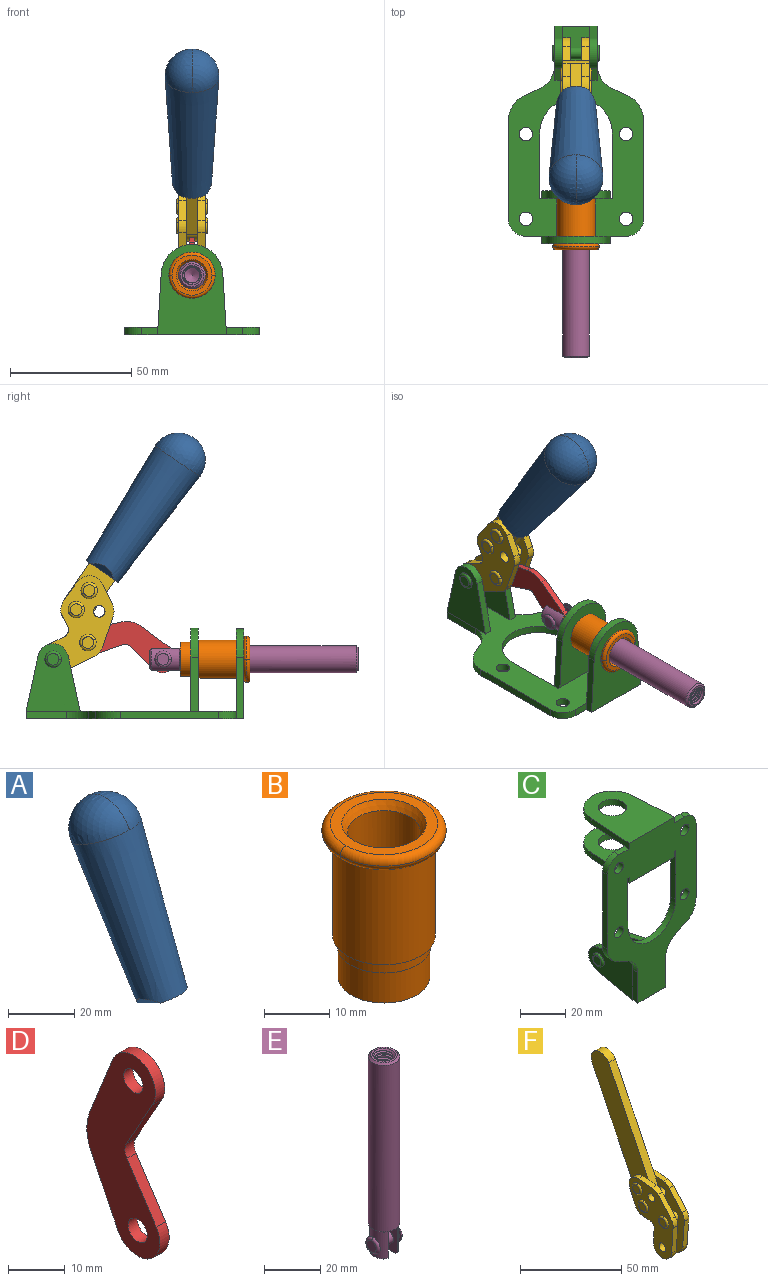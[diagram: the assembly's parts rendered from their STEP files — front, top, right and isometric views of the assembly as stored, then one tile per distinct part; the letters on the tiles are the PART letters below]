
ASSEMBLY  parts=6 mates=6
PART A: 11 faces, bbox 22.3x42.6x64.5 mm
  f0: sphere r=11.13mm, area 411.4mm2, adj f1,f8
  f1: cone r=11.11mm half-angle=3.3deg, axis (0,0.44,0.9), area 3251.8mm2, adj f0,f7,f8,f9,f10
  f2: cylinder r=6.16mm len=11.7mm, axis (1,0,0), area 89.5mm2, adj f3,f4,f5,f6
  f3: plane 60.23x36.75mm, normal (-1,0,0), area 763.6mm2, adj f2,f4,f6,f10
  f4: plane 51.37x25.05mm, normal (0,0.9,-0.44), area 264.2mm2, adj f2,f3,f5,f10
  f5: plane 60.23x36.75mm, normal (1,0,0), area 763.6mm2, adj f2,f4,f6,f10
  f6: plane 51.37x25.05mm, normal (0,-0.9,0.44), area 264.2mm2, adj f2,f3,f5,f10
  f7: plane 9.95x5.95mm, normal (0.71,-0.31,-0.64), area 25.8mm2, adj f1,f10
  f8: sphere r=11.13mm, area 411.4mm2, adj f0,f1
  f9: plane 9.95x5.95mm, normal (-0.71,-0.31,-0.64), area 25.8mm2, adj f1,f10
  f10: plane 14.27x11.38mm, normal (0,-0.44,-0.9), area 106.7mm2, adj f1,f3,f4,f5,f6,f7,f9
PART B: 15 faces, bbox 20.6x20.6x28.7 mm
  f0: torus R=8.26mm, axis (0,0,1), area 56.8mm2, adj f1,f10,f12
  f1: torus R=8.26mm, axis (0,0,1), area 56.8mm2, adj f0,f6,f13
  f2: cylinder r=5.59mm len=25.91mm, axis (0,0,1), area 909.6mm2, adj f3,f4
  f3: cone r=6.86mm half-angle=45deg, axis (0,0,-1), area 70.2mm2, adj f2,f14
  f4: cone r=6.47mm half-angle=30deg, axis (0,0,1), area 66.7mm2, adj f2,f13
  f5: cylinder r=7.04mm len=14.07mm, axis (0,0,1), area 252.6mm2, adj f11,f14
  f6: torus R=8.26mm, axis (0,0,1), area 56.8mm2, adj f1,f12,f13
  f7: cylinder r=7.16mm len=14.33mm, axis (0,0,1), area 91.5mm2, adj f9,f11
  f8: cylinder r=7.86mm len=18.42mm, axis (0,0,1), area 909.6mm2, adj f9,f10
  f9: plane 15.72x15.72mm, normal (0,0,-1), area 33mm2, adj f7,f8
  f10: plane 16.51x16.51mm, normal (0,0,-1), area 19.9mm2, adj f0,f8,f12
  f11: plane 14.33x14.33mm, normal (0,0,-1), area 5.7mm2, adj f5,f7
  f12: torus R=8.26mm, axis (0,0,1), area 56.8mm2, adj f0,f6,f10
  f13: plane 16.51x16.51mm, normal (0,0,1), area 82.7mm2, adj f1,f4,f6
  f14: plane 14.07x14.07mm, normal (0,0,-1), area 7.8mm2, adj f3,f5
PART C: 55 faces, bbox 55.7x37.4x89.8 mm
  f0: torus R=2.41mm, axis (-1,0,0), area 15mm2, adj f11,f15,f25
  f1: torus R=2.41mm, axis (-1,0,0), area 15mm2, adj f10,f12,f22
  f2: cylinder r=2.78mm len=5.56mm, axis (0,-1,0), area 54.2mm2, adj f30,f54
  f3: cylinder r=14.99mm len=29.97mm, axis (0,-1,0), area 145.9mm2, adj f30,f49,f53,f54
  f4: cylinder r=2.78mm len=5.56mm, axis (0,-1,0), area 54.2mm2, adj f30,f54
  f5: cylinder r=2.78mm len=5.56mm, axis (0,-1,0), area 54.2mm2, adj f30,f54
  f6: cylinder r=2.78mm len=5.56mm, axis (0,-1,0), area 54.2mm2, adj f30,f54
  f7: cylinder r=6.35mm len=12.7mm, axis (0,0,1), area 123.6mm2, adj f27,f51
  f8: cylinder r=6.35mm len=12.7mm, axis (0,0,-1), area 124.7mm2, adj f21,f35
  f9: cylinder r=2.41mm len=11.18mm, axis (-1,0,0), area 169.4mm2, adj f16,f19
  f10: plane 4.83x4.83mm, normal (1,0,0), area 18.3mm2, adj f1,f12
  f11: plane 4.83x4.83mm, normal (-1,0,0), area 18.3mm2, adj f0,f15
  f12: torus R=2.41mm, axis (-1,0,0), area 15mm2, adj f1,f10,f22
  f13: cylinder r=6.35mm len=12.41mm, axis (1,0,0), area 53.4mm2, adj f18,f19,f22,f23
  f14: cylinder r=6.35mm len=12.41mm, axis (-1,0,0), area 53.4mm2, adj f16,f17,f24,f25
  f15: torus R=2.41mm, axis (-1,0,0), area 15mm2, adj f0,f11,f25
  f16: plane 27.86x22.35mm, normal (1,0,0), area 425.4mm2, adj f9,f14,f17,f24,f30
  f17: plane 22.86x4.97mm, normal (0,0.21,0.98), area 72.5mm2, adj f14,f16,f25,f30
  f18: plane 22.86x4.97mm, normal (0,0.21,0.98), area 72.5mm2, adj f13,f19,f22,f30
  f19: plane 27.86x22.35mm, normal (-1,0,0), area 425.4mm2, adj f9,f13,f18,f23,f30
  f20: cylinder r=12.7mm len=25.35mm, axis (0,0,-1), area 119.8mm2, adj f21,f34,f35,f36
  f21: plane 34.21x28.07mm, normal (0,0,-1), area 702.4mm2, adj f8,f20,f30,f34,f36
  f22: plane 27.96x22.45mm, normal (1,0,0), area 407.2mm2, adj f1,f12,f13,f18,f23,f30,f42,f43
  f23: plane 22.86x4.97mm, normal (0,0.21,-0.98), area 72.5mm2, adj f13,f19,f22,f44
  f24: plane 22.86x4.97mm, normal (0,0.21,-0.98), area 72.5mm2, adj f14,f16,f25,f44
  f25: plane 27.86x22.35mm, normal (-1,0,0), area 407.1mm2, adj f0,f14,f15,f17,f24,f30,f45,f46
  f26: plane 3.1x0.95mm, normal (0,0,-1), area 2.7mm2, adj f30,f49,f50,f54
  f27: plane 34.21x28.07mm, normal (0,0,1), area 702.4mm2, adj f7,f28,f30,f50,f52
  f28: cylinder r=12.7mm len=25.35mm, axis (0,0,1), area 118.8mm2, adj f27,f50,f51,f52
  f29: plane 3.1x0.95mm, normal (0,0,-1), area 2.7mm2, adj f30,f52,f53,f54
  f30: plane 86.54x55.63mm, normal (0,1,0), area 2362.9mm2, adj f2,f3,f4,f5,f6,f16,f17,f18
  f31: plane 40.56x3.1mm, normal (-1,0,0), area 125.7mm2, adj f30,f32,f48,f54
  f32: cylinder r=7.11mm len=7.11mm, axis (0,-1,0), area 34.6mm2, adj f30,f31,f33,f54
  f33: plane 6.67x3.1mm, normal (0,0,1), area 20.4mm2, adj f30,f32,f34,f54
  f34: plane 25.39x3.13mm, normal (-1,0.06,0), area 79.5mm2, adj f20,f21,f33,f35,f54
  f35: plane 37.31x28.45mm, normal (0,0,1), area 789.9mm2, adj f8,f20,f34,f36,f54
  f36: plane 25.39x3.13mm, normal (1,0.06,0), area 79.5mm2, adj f20,f21,f35,f37,f54
  f37: plane 6.67x3.1mm, normal (0,0,1), area 20.4mm2, adj f30,f36,f38,f54
  f38: cylinder r=7.11mm len=7.11mm, axis (0,-1,0), area 34.6mm2, adj f30,f37,f39,f54
  f39: plane 40.56x3.1mm, normal (1,0,0), area 125.7mm2, adj f30,f38,f40,f54
  f40: cylinder r=11.18mm len=10.16mm, axis (0,-1,0), area 39.5mm2, adj f30,f39,f41,f54
  f41: plane 6.09x3.1mm, normal (0.42,0,-0.91), area 20.8mm2, adj f30,f40,f42,f54
  f42: cylinder r=11.18mm len=9.41mm, axis (0,-1,0), area 37.2mm2, adj f22,f30,f41,f43,f54
  f43: plane 16.5x3.1mm, normal (1,0,0), area 51.1mm2, adj f22,f42,f44,f54
  f44: plane 17.37x3.1mm, normal (0,0,-1), area 53.8mm2, adj f23,f24,f30,f43,f45,f54
  f45: plane 16.5x3.1mm, normal (-1,0,0), area 51.1mm2, adj f25,f44,f46,f54
  f46: cylinder r=11.18mm len=9.41mm, axis (0,-1,0), area 37.2mm2, adj f25,f30,f45,f47,f54
  f47: plane 6.09x3.1mm, normal (-0.42,0,-0.91), area 20.8mm2, adj f30,f46,f48,f54
  f48: cylinder r=11.18mm len=10.16mm, axis (0,-1,0), area 39.5mm2, adj f30,f31,f47,f54
  f49: plane 26.54x3.1mm, normal (-1,0,0), area 82.3mm2, adj f3,f26,f30,f54
  f50: plane 25.39x3.1mm, normal (1,0.06,0), area 78.8mm2, adj f26,f27,f28,f51,f54
  f51: plane 37.31x28.45mm, normal (0,0,-1), area 789.9mm2, adj f7,f28,f50,f52,f54
  f52: plane 25.39x3.1mm, normal (-1,0.06,0), area 78.8mm2, adj f27,f28,f29,f51,f54
  f53: plane 26.54x3.1mm, normal (1,0,0), area 82.3mm2, adj f3,f29,f30,f54
  f54: plane 89.66x55.63mm, normal (0,-1,0), area 2678.5mm2, adj f2,f3,f4,f5,f6,f26,f29,f31
PART D: 12 faces, bbox 2.3x18.2x42.8 mm
  f0: cylinder r=2.4mm len=4.8mm, axis (1,0,0), area 34.9mm2, adj f4,f11
  f1: cylinder r=10.41mm len=8.47mm, axis (1,0,0), area 20.2mm2, adj f4,f9,f10,f11
  f2: cylinder r=3.05mm len=3.16mm, axis (1,0,0), area 7.7mm2, adj f4,f6,f7,f11
  f3: cylinder r=2.4mm len=4.8mm, axis (1,0,0), area 34.9mm2, adj f4,f11
  f4: plane 42.81x18.23mm, normal (-1,0,0), area 414.1mm2, adj f0,f1,f2,f3,f5,f6,f7,f8
  f5: cylinder r=5.54mm len=10.67mm, axis (1,0,0), area 41.8mm2, adj f4,f6,f10,f11
  f6: plane 11.66x6.53mm, normal (0,-0.87,-0.49), area 30.9mm2, adj f2,f4,f5,f11
  f7: plane 11.17x7.33mm, normal (0,-0.84,0.55), area 30.9mm2, adj f2,f4,f8,f11
  f8: cylinder r=5.54mm len=10.51mm, axis (1,0,0), area 41.8mm2, adj f4,f7,f9,f11
  f9: plane 13.67x6.67mm, normal (0,0.9,-0.44), area 35.1mm2, adj f1,f4,f8,f11
  f10: plane 14.1x5.7mm, normal (0,0.93,0.37), area 35.1mm2, adj f1,f4,f5,f11
  f11: plane 42.81x18.23mm, normal (1,0,0), area 414.1mm2, adj f0,f1,f2,f3,f5,f6,f7,f8
PART E: 48 faces, bbox 12.6x11.1x86.1 mm
  f0: torus R=2.41mm, axis (-1,0,0), area 15mm2, adj f30,f32,f34
  f1: torus R=2.41mm, axis (-1,0,0), area 15mm2, adj f29,f31,f33
  f2: cylinder r=5.54mm len=72.39mm, axis (0,0,1), area 2518.5mm2, adj f3,f4,f42,f43
  f3: cone r=5.54mm half-angle=45deg, axis (0,0,1), area 7.6mm2, adj f2,f5,f41
  f4: cone r=5.54mm half-angle=45deg, axis (0,0,-1), area 34.9mm2, adj f2,f39
  f5: cylinder r=5.08mm len=11.48mm, axis (0,0,1), area 108.3mm2, adj f3,f7,f8,f41
  f6: cylinder r=2.41mm len=4.83mm, axis (-1,0,0), area 71.2mm2, adj f40,f41
  f7: cylinder r=2.41mm len=4.83mm, axis (-1,0,0), area 7.6mm2, adj f5,f34
  f8: cone r=5.08mm half-angle=45deg, axis (0,0,1), area 10.6mm2, adj f5,f37,f41
  f9: cone r=3.98mm half-angle=45deg, axis (0,0,1), area 17.6mm2, adj f27,f39,f45,f46,f47
  f10: cylinder r=2.41mm len=4.83mm, axis (-1,0,0), area 7.6mm2, adj f33,f38
  f11: cylinder r=3.2mm len=6.4mm, axis (0,0,1), area 78.4mm2, adj f12,f28,f44,f45,f47
  f12: cylinder r=3.2mm len=6.4mm, axis (0,0,1), area 10.5mm2, adj f11,f13,f45,f47
  f13: cylinder r=3.2mm len=6.4mm, axis (0,0,1), area 10.5mm2, adj f12,f14,f45,f47
  f14: cylinder r=3.2mm len=6.4mm, axis (0,0,1), area 10.5mm2, adj f13,f15,f45,f47
  f15: cylinder r=3.2mm len=6.4mm, axis (0,0,1), area 10.5mm2, adj f14,f16,f45,f47
  f16: cylinder r=3.2mm len=6.4mm, axis (0,0,1), area 10.5mm2, adj f15,f17,f45,f47
  f17: cylinder r=3.2mm len=6.4mm, axis (0,0,1), area 10.5mm2, adj f16,f18,f45,f47
  f18: cylinder r=3.2mm len=6.4mm, axis (0,0,1), area 10.5mm2, adj f17,f19,f45,f47
  f19: cylinder r=3.2mm len=6.4mm, axis (0,0,1), area 10.5mm2, adj f18,f20,f45,f47
  f20: cylinder r=3.2mm len=6.4mm, axis (0,0,1), area 10.5mm2, adj f19,f21,f45,f47
  f21: cylinder r=3.2mm len=6.4mm, axis (0,0,1), area 10.5mm2, adj f20,f22,f45,f47
  f22: cylinder r=3.2mm len=6.4mm, axis (0,0,1), area 10.5mm2, adj f21,f23,f45,f47
  f23: cylinder r=3.2mm len=6.4mm, axis (0,0,1), area 10.5mm2, adj f22,f24,f45,f47
  f24: cylinder r=3.2mm len=6.4mm, axis (0,0,1), area 10.5mm2, adj f23,f25,f45,f47
  f25: cylinder r=3.2mm len=6.4mm, axis (0,0,1), area 10.5mm2, adj f24,f26,f45,f47
  f26: cylinder r=3.2mm len=6.4mm, axis (0,0,1), area 10.5mm2, adj f25,f27,f45,f47
  f27: cylinder r=3.2mm len=6.4mm, axis (0,0,1), area 7.4mm2, adj f9,f26,f45,f47
  f28: cone r=3.2mm half-angle=60deg, axis (0,0,1), area 37.2mm2, adj f11
  f29: plane 4.83x4.83mm, normal (-1,0,0), area 18.3mm2, adj f1,f31
  f30: plane 4.83x4.83mm, normal (1,0,0), area 18.3mm2, adj f0,f32
  f31: torus R=2.41mm, axis (-1,0,0), area 15mm2, adj f1,f29,f33
  f32: torus R=2.41mm, axis (-1,0,0), area 15mm2, adj f0,f30,f34
  f33: plane 6.83x6.83mm, normal (1,0,0), area 18.3mm2, adj f1,f10,f31
  f34: plane 6.83x6.83mm, normal (-1,0,0), area 18.3mm2, adj f0,f7,f32
  f35: cone r=5.08mm half-angle=45deg, axis (0,0,1), area 10.6mm2, adj f36,f38,f40
  f36: plane 7.25x1.97mm, normal (0,0,-1), area 10mm2, adj f35,f40
  f37: plane 7.25x1.97mm, normal (0,0,-1), area 10mm2, adj f8,f41
  f38: cylinder r=5.08mm len=11.48mm, axis (0,0,1), area 108.3mm2, adj f10,f35,f40,f42
  f39: plane 9.55x9.55mm, normal (0,0,1), area 22mm2, adj f4,f9
  f40: plane 12.76x10.09mm, normal (1,0,0), area 95.7mm2, adj f6,f35,f36,f38,f42,f43
  f41: plane 12.76x10.09mm, normal (-1,0,0), area 95.7mm2, adj f3,f5,f6,f8,f37,f43
  f42: cone r=5.54mm half-angle=45deg, axis (0,0,1), area 7.6mm2, adj f2,f38,f40
  f43: plane 11.07x4.7mm, normal (0,0,-1), area 50.4mm2, adj f2,f40,f41
  f44: plane 0.89x0.62mm, normal (-1,0,0), area 0.3mm2, adj f11,f45,f46,f47
  f45: bspline ~24.8x7.63mm, area 266.6mm2, adj f9,f11,f12,f13,f14,f15,f16,f17
  f46: bspline ~24.87x7.63mm, area 73.6mm2, adj f9,f44,f45,f47
  f47: bspline ~24.98x7.63mm, area 272.5mm2, adj f9,f11,f12,f13,f14,f15,f16,f17
PART F: 59 faces, bbox 12.9x60.2x99.6 mm
  f0: torus R=2.39mm, axis (-1,0,0), area 14.9mm2, adj f20,f43,f51
  f1: torus R=2.39mm, axis (-1,0,0), area 14.9mm2, adj f19,f42,f51
  f2: torus R=2.39mm, axis (-1,0,0), area 14.9mm2, adj f18,f35,f51
  f3: torus R=2.39mm, axis (-1,0,0), area 14.9mm2, adj f14,f17,f23
  f4: torus R=2.39mm, axis (-1,0,0), area 14.9mm2, adj f13,f16,f23
  f5: torus R=2.39mm, axis (-1,0,0), area 14.9mm2, adj f12,f15,f23
  f6: cylinder r=2.39mm len=4.78mm, axis (1,0,0), area 46.5mm2, adj f48,f50,f51
  f7: cylinder r=2.39mm len=4.78mm, axis (1,0,0), area 46.5mm2, adj f50,f51
  f8: cylinder r=6.35mm len=12.68mm, axis (1,0,0), area 61.8mm2, adj f38,f39,f50,f51
  f9: cylinder r=2.39mm len=4.78mm, axis (-1,0,0), area 70.5mm2, adj f46,f50
  f10: cylinder r=2.39mm len=4.78mm, axis (-1,0,0), area 46.5mm2, adj f23,f45,f46
  f11: cylinder r=2.39mm len=4.78mm, axis (-1,0,0), area 46.5mm2, adj f23,f46
  f12: plane 4.78x4.78mm, normal (1,0,0), area 17.9mm2, adj f5,f15
  f13: plane 4.78x4.78mm, normal (1,0,0), area 17.9mm2, adj f4,f16
  f14: plane 4.78x4.78mm, normal (1,0,0), area 17.9mm2, adj f3,f17
  f15: torus R=2.39mm, axis (-1,0,0), area 14.9mm2, adj f5,f12,f23
  f16: torus R=2.39mm, axis (-1,0,0), area 14.9mm2, adj f4,f13,f23
  f17: torus R=2.39mm, axis (-1,0,0), area 14.9mm2, adj f3,f14,f23
  f18: plane 4.78x4.78mm, normal (-1,0,0), area 17.9mm2, adj f2,f35
  f19: plane 4.78x4.78mm, normal (-1,0,0), area 17.9mm2, adj f1,f42
  f20: plane 4.78x4.78mm, normal (-1,0,0), area 17.9mm2, adj f0,f43
  f21: plane 2.26x0.2mm, normal (1,0,0), area 0.2mm2, adj f31,f44
  f22: plane 2.26x0.2mm, normal (-1,0,0), area 0.2mm2, adj f41,f44
  f23: plane 39.37x30.77mm, normal (1,0,0), area 565.5mm2, adj f3,f4,f5,f10,f11,f15,f16,f17
  f24: cylinder r=6.1mm len=4.15mm, axis (-1,0,0), area 14.7mm2, adj f23,f25,f32,f46
  f25: plane 10.25x9.01mm, normal (0,-0.75,0.66), area 42.3mm2, adj f23,f24,f26,f46
  f26: cylinder r=6.35mm len=4.64mm, axis (-1,0,0), area 15.6mm2, adj f23,f25,f27,f46
  f27: plane 15.84x3.1mm, normal (0,-1,-0.07), area 49.2mm2, adj f23,f26,f28,f46
  f28: cylinder r=6.35mm len=12.68mm, axis (-1,0,0), area 61.8mm2, adj f23,f27,f29,f46
  f29: plane 8.11x3.1mm, normal (0,1,0.07), area 25.2mm2, adj f23,f28,f30,f46
  f30: cylinder r=3.05mm len=3.25mm, axis (-1,0,0), area 14.8mm2, adj f23,f29,f31,f46
  f31: plane 5.99x3.1mm, normal (0,0.07,-1), area 18.6mm2, adj f21,f23,f30,f44,f46
  f32: plane 9.5x3.1mm, normal (0,-0.07,1), area 29.5mm2, adj f23,f24,f33,f46,f47
  f33: cylinder r=6.1mm len=8.63mm, axis (-1,0,0), area 39.1mm2, adj f23,f32,f34,f47
  f34: plane 8.65x3.96mm, normal (0,0.91,-0.42), area 29.5mm2, adj f23,f33,f44,f47
  f35: torus R=2.39mm, axis (-1,0,0), area 14.9mm2, adj f2,f18,f51
  f36: plane 10.25x9.01mm, normal (0,-0.75,0.66), area 42.3mm2, adj f37,f49,f50,f51
  f37: cylinder r=6.35mm len=4.64mm, axis (1,0,0), area 15.6mm2, adj f36,f38,f50,f51
  f38: plane 15.84x3.1mm, normal (0,-1,-0.07), area 49.2mm2, adj f8,f37,f50,f51
  f39: plane 8.11x3.1mm, normal (0,1,0.07), area 25.2mm2, adj f8,f40,f50,f51
  f40: cylinder r=3.05mm len=3.25mm, axis (1,0,0), area 14.8mm2, adj f39,f41,f50,f51
  f41: plane 5.99x3.1mm, normal (0,0.07,-1), area 18.6mm2, adj f22,f40,f44,f50,f51
  f42: torus R=2.39mm, axis (-1,0,0), area 14.9mm2, adj f1,f19,f51
  f43: torus R=2.39mm, axis (-1,0,0), area 14.9mm2, adj f0,f20,f51
  f44: cylinder r=6.35mm len=12.12mm, axis (-1,0,0), area 128.9mm2, adj f21,f22,f23,f31,f34,f41,f46,f47
  f45: plane 2.65x1.35mm, normal (1,0,0), area 1mm2, adj f10,f55
  f46: plane 39.08x20.42mm, normal (-1,0,0), area 412.5mm2, adj f9,f10,f11,f24,f25,f26,f27,f28
  f47: plane 77.62x39.82mm, normal (1,0,0), area 850mm2, adj f32,f33,f34,f44,f53,f54,f55
  f48: plane 2.65x1.35mm, normal (-1,0,0), area 1mm2, adj f6,f55
  f49: cylinder r=6.1mm len=4.15mm, axis (1,0,0), area 14.7mm2, adj f36,f50,f51,f56
  f50: plane 39.08x20.42mm, normal (1,0,0), area 412.5mm2, adj f6,f7,f8,f9,f36,f37,f38,f39
  f51: plane 39.37x30.77mm, normal (-1,0,0), area 565.5mm2, adj f0,f1,f2,f6,f7,f8,f35,f36
  f52: plane 8.65x3.96mm, normal (0,0.91,-0.42), area 29.5mm2, adj f44,f51,f57,f58
  f53: plane 68.49x33.4mm, normal (0,0.9,-0.44), area 358.1mm2, adj f44,f47,f54,f58
  f54: cylinder r=6.35mm len=12.06mm, axis (1,0,0), area 93.7mm2, adj f47,f53,f55,f58
  f55: plane 68.49x33.4mm, normal (0,-0.9,0.44), area 358.1mm2, adj f44,f45,f46,f47,f48,f50,f54,f58
  f56: plane 9.5x3.1mm, normal (0,-0.07,1), area 29.5mm2, adj f49,f50,f51,f57,f58
  f57: cylinder r=6.1mm len=8.63mm, axis (1,0,0), area 39.1mm2, adj f51,f52,f56,f58
  f58: plane 77.62x39.82mm, normal (-1,0,0), area 850mm2, adj f44,f52,f53,f54,f55,f56,f57
PLACE A rot(axis=(1,0,0),60.3deg) t=(0,1.16,19.14)mm
PLACE B rot(axis=(1,0,0),90deg) t=(0,9.14,0)mm
PLACE C rot(axis=(1,0,0),90deg) t=(0,9.14,0)mm fixed
PLACE D rot(axis=(1,0,0),104.5deg) t=(0,17.09,4.67)mm
PLACE E rot(axis=(1,0,0),90deg) t=(0,11.41,0)mm
PLACE F rot(axis=(1,0,0),60.3deg) t=(0,1.16,19.14)mm
MATE fastened F.f54 <-> A.f2  axis (1,0,0) through (0,-11.22,107.98)mm
MATE revolute F.f7 <-> C.f0  axis (1,0,0) through (0,41.23,24.61)mm
MATE fastened B.f0 <-> C.f7  axis (0,1,0) through (0,-37.25,24.61)mm
MATE revolute D.f3 <-> F.f4  axis (1,0,0) through (0,26.93,31.5)mm
MATE slider E.f2 <-> C.f7  axis (0,-1,0) through (0,-47.37,24.61)mm
MATE revolute D.f5 <-> E.f6  axis (1,0,0) through (0,-4.07,24.61)mm
